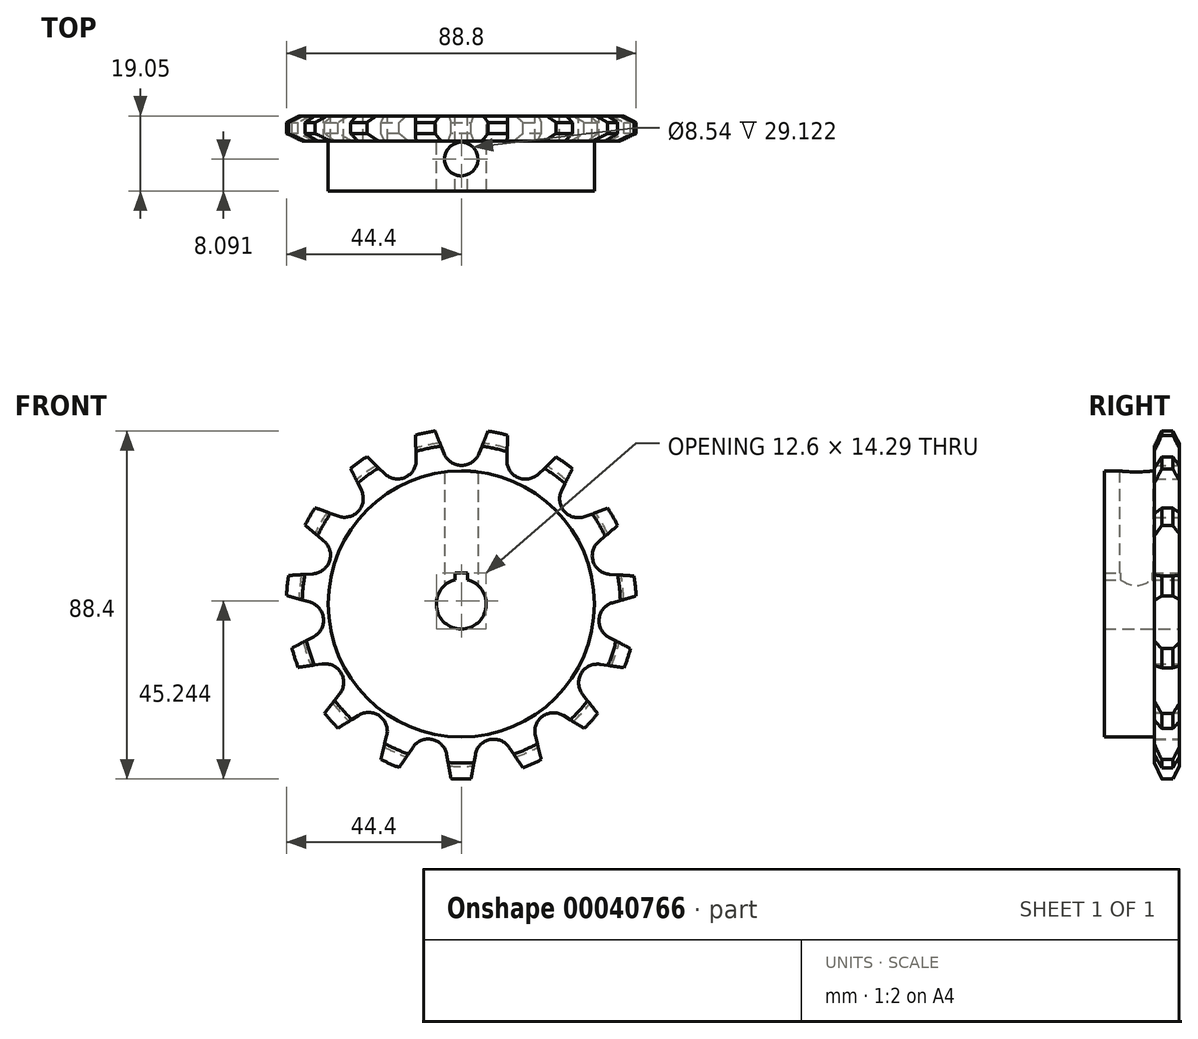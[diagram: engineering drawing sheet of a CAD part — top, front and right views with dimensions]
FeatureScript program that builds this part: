
annotation { "Feature Type Name" : "Feature", "Feature Type Description" : "" }
export const myFeature = defineFeature(function(context is Context, id is Id, definition is map)
    precondition{}
    {
        {
            var Q0;
            Q0=qCreatedBy(makeId("Front.planeOp"),FACE);
            var sketch = newSketch(context, id + "F0", { "sketchPlane" : qUnion([Q0])});
            skArc(sketch, "E0", {"start": v(-6.66, 43.95) * mm, "mid": v(-9.18, 43.5) * mm, "end": v(-11.66, 42.9) * mm});
            skArc(sketch, "E1", {"start": v(-4.34, 38.18) * mm, "mid": v(0.07, 35.2) * mm, "end": v(4.48, 38.18) * mm});
            skLineSegment(sketch, "E2", {"start": v(4.48, 38.18) * mm, "end": v(6.79, 43.93) * mm});
            skLineSegment(sketch, "E3", {"start": v(-4.34, 38.18) * mm, "end": v(-6.66, 43.95) * mm});
            skLineSegment(sketch, "E4.1.0", {"start": v(-19.5, 33.12) * mm, "end": v(-23.96, 37.44) * mm});
            skArc(sketch, "E4.1.1", {"start": v(-19.5, 33.12) * mm, "mid": v(-14.26, 32.19) * mm, "end": v(-11.44, 36.7) * mm});
            skLineSegment(sketch, "E4.1.2", {"start": v(-11.44, 36.7) * mm, "end": v(-11.66, 42.9) * mm});
            skLineSegment(sketch, "E4.2.0", {"start": v(-31.28, 22.32) * mm, "end": v(-37.12, 24.45) * mm});
            skArc(sketch, "E4.2.1", {"start": v(-31.28, 22.32) * mm, "mid": v(-26.12, 23.6) * mm, "end": v(-25.38, 28.88) * mm});
            skLineSegment(sketch, "E4.2.2", {"start": v(-25.38, 28.88) * mm, "end": v(-28.1, 34.44) * mm});
            skLineSegment(sketch, "E4.3.0", {"start": v(-37.66, 7.67) * mm, "end": v(-43.86, 7.24) * mm});
            skArc(sketch, "E4.3.1", {"start": v(-37.66, 7.67) * mm, "mid": v(-33.46, 10.94) * mm, "end": v(-34.93, 16.06) * mm});
            skLineSegment(sketch, "E4.3.2", {"start": v(-34.93, 16.06) * mm, "end": v(-39.68, 20.03) * mm});
            skLineSegment(sketch, "E4.4.0", {"start": v(-37.52, -8.31) * mm, "end": v(-43.01, -11.22) * mm});
            skArc(sketch, "E4.4.1", {"start": v(-37.52, -8.31) * mm, "mid": v(-35.02, -3.61) * mm, "end": v(-38.44, 0.46) * mm});
            skLineSegment(sketch, "E4.4.2", {"start": v(-38.44, 0.46) * mm, "end": v(-44.4, 2.16) * mm});
            skLineSegment(sketch, "E4.5.0", {"start": v(-30.9, -22.85) * mm, "end": v(-34.73, -27.75) * mm});
            skArc(sketch, "E4.5.1", {"start": v(-30.9, -22.85) * mm, "mid": v(-30.52, -17.55) * mm, "end": v(-35.3, -15.22) * mm});
            skLineSegment(sketch, "E4.5.2", {"start": v(-35.3, -15.22) * mm, "end": v(-41.44, -16.08) * mm});
            skLineSegment(sketch, "E4.6.0", {"start": v(-18.93, -33.44) * mm, "end": v(-20.44, -39.47) * mm});
            skArc(sketch, "E4.6.1", {"start": v(-18.93, -33.44) * mm, "mid": v(-20.75, -28.44) * mm, "end": v(-26.06, -28.26) * mm});
            skLineSegment(sketch, "E4.6.2", {"start": v(-26.06, -28.26) * mm, "end": v(-31.31, -31.55) * mm});
            skLineSegment(sketch, "E4.7.0", {"start": v(-3.7, -38.25) * mm, "end": v(-2.62, -44.37) * mm});
            skArc(sketch, "E4.7.1", {"start": v(-3.7, -38.25) * mm, "mid": v(-7.38, -34.42) * mm, "end": v(-12.32, -36.42) * mm});
            skLineSegment(sketch, "E4.7.2", {"start": v(-12.32, -36.42) * mm, "end": v(-15.77, -41.56) * mm});
            skLineSegment(sketch, "E4.8.0", {"start": v(12.19, -36.45) * mm, "end": v(15.66, -41.6) * mm});
            skArc(sketch, "E4.8.1", {"start": v(12.19, -36.45) * mm, "mid": v(7.25, -34.45) * mm, "end": v(3.56, -38.28) * mm});
            skLineSegment(sketch, "E4.8.2", {"start": v(3.56, -38.28) * mm, "end": v(2.5, -44.38) * mm});
            skLineSegment(sketch, "E4.9.0", {"start": v(25.96, -28.34) * mm, "end": v(31.22, -31.64) * mm});
            skArc(sketch, "E4.9.1", {"start": v(25.96, -28.34) * mm, "mid": v(20.64, -28.52) * mm, "end": v(18.82, -33.52) * mm});
            skLineSegment(sketch, "E4.9.2", {"start": v(18.82, -33.52) * mm, "end": v(20.33, -39.53) * mm});
            skLineSegment(sketch, "E4.10.0", {"start": v(35.24, -15.33) * mm, "end": v(41.4, -16.2) * mm});
            skArc(sketch, "E4.10.1", {"start": v(35.24, -15.33) * mm, "mid": v(30.46, -17.66) * mm, "end": v(30.83, -22.97) * mm});
            skLineSegment(sketch, "E4.10.2", {"start": v(30.83, -22.97) * mm, "end": v(34.65, -27.84) * mm});
            skLineSegment(sketch, "E4.11.0", {"start": v(38.43, 0.33) * mm, "end": v(44.4, 2.03) * mm});
            skArc(sketch, "E4.11.1", {"start": v(38.43, 0.33) * mm, "mid": v(35, -3.75) * mm, "end": v(37.5, -8.44) * mm});
            skLineSegment(sketch, "E4.11.2", {"start": v(37.5, -8.44) * mm, "end": v(42.98, -11.34) * mm});
            skLineSegment(sketch, "E4.12.0", {"start": v(34.97, 15.93) * mm, "end": v(39.74, 19.92) * mm});
            skArc(sketch, "E4.12.1", {"start": v(34.97, 15.93) * mm, "mid": v(33.5, 10.82) * mm, "end": v(37.7, 7.54) * mm});
            skLineSegment(sketch, "E4.12.2", {"start": v(37.7, 7.54) * mm, "end": v(43.88, 7.12) * mm});
            skLineSegment(sketch, "E4.13.0", {"start": v(25.47, 28.78) * mm, "end": v(28.2, 34.36) * mm});
            skArc(sketch, "E4.13.1", {"start": v(25.47, 28.78) * mm, "mid": v(26.2, 23.5) * mm, "end": v(31.37, 22.22) * mm});
            skLineSegment(sketch, "E4.13.2", {"start": v(31.37, 22.22) * mm, "end": v(37.19, 24.35) * mm});
            skLineSegment(sketch, "E4.14.0", {"start": v(11.56, 36.65) * mm, "end": v(11.79, 42.86) * mm});
            skArc(sketch, "E4.14.1", {"start": v(11.56, 36.65) * mm, "mid": v(14.38, 32.13) * mm, "end": v(19.62, 33.06) * mm});
            skLineSegment(sketch, "E4.14.2", {"start": v(19.62, 33.06) * mm, "end": v(24.07, 37.37) * mm});
            skArc(sketch, "E5.trimOffspring", {"start": v(-23.96, 37.44) * mm, "mid": v(-26.08, 36) * mm, "end": v(-28.1, 34.44) * mm});
            skArc(sketch, "E6.trimOffspring", {"start": v(-37.12, 24.45) * mm, "mid": v(-38.46, 22.28) * mm, "end": v(-39.68, 20.03) * mm});
            skArc(sketch, "E7.trimOffspring", {"start": v(11.79, 42.86) * mm, "mid": v(9.3, 43.47) * mm, "end": v(6.79, 43.93) * mm});
            skArc(sketch, "E8.trimOffspring", {"start": v(28.2, 34.36) * mm, "mid": v(26.18, 35.92) * mm, "end": v(24.07, 37.37) * mm});
            skArc(sketch, "E9.trimOffspring", {"start": v(39.74, 19.92) * mm, "mid": v(38.53, 22.17) * mm, "end": v(37.19, 24.35) * mm});
            skArc(sketch, "E10.trimOffspring", {"start": v(44.4, 2.03) * mm, "mid": v(44.21, 4.58) * mm, "end": v(43.88, 7.12) * mm});
            skArc(sketch, "E11.trimOffspring", {"start": v(41.4, -16.2) * mm, "mid": v(42.25, -13.8) * mm, "end": v(42.98, -11.34) * mm});
            skArc(sketch, "E12.trimOffspring", {"start": v(31.22, -31.64) * mm, "mid": v(33, -29.79) * mm, "end": v(34.65, -27.84) * mm});
            skArc(sketch, "E13.trimOffspring", {"start": v(15.66, -41.6) * mm, "mid": v(18.02, -40.63) * mm, "end": v(20.33, -39.53) * mm});
            skArc(sketch, "E14.trimOffspring", {"start": v(-2.62, -44.37) * mm, "mid": v(-0.06, -44.45) * mm, "end": v(2.5, -44.38) * mm});
            skArc(sketch, "E15.trimOffspring", {"start": v(-20.44, -39.47) * mm, "mid": v(-18.14, -40.58) * mm, "end": v(-15.77, -41.56) * mm});
            skArc(sketch, "E16.trimOffspring", {"start": v(-34.73, -27.75) * mm, "mid": v(-33.07, -29.7) * mm, "end": v(-31.31, -31.55) * mm});
            skArc(sketch, "E17.trimOffspring", {"start": v(-43.01, -11.22) * mm, "mid": v(-42.3, -13.68) * mm, "end": v(-41.44, -16.08) * mm});
            skArc(sketch, "E18.trimOffspring", {"start": v(-43.86, 7.24) * mm, "mid": v(-44.2, 4.7) * mm, "end": v(-44.4, 2.16) * mm});
            skSolve(sketch);
        }
        {
            var Q0;
            Q0 = qSketchRegion(id + "F0", true);
            extrude(context, id + "F1", {"entities" : qUnion([Q0]), "depth" : 6.35 * mm});
        }
        {
            var Q0;
            Q0=qCreatedBy(makeId("Right.planeOp"),FACE);
            var sketch = newSketch(context, id + "F2", { "sketchPlane" : qUnion([Q0])});
            skLineSegment(sketch, "E19", {"start": v(-4.11, 45.22) * mm, "end": v(-2.04, 45.22) * mm});
            skLineSegment(sketch, "E20", {"start": v(-2.04, 45.22) * mm, "end": v(0.8, 39.7) * mm});
            skLineSegment(sketch, "E21", {"start": v(-4.11, 45.22) * mm, "end": v(-7.04, 38.94) * mm});
            skLineSegment(sketch, "E22", {"start": v(-7.04, 38.94) * mm, "end": v(-6.55, 46.64) * mm});
            skLineSegment(sketch, "E23", {"start": v(-6.55, 46.64) * mm, "end": v(0.85, 46.64) * mm});
            skLineSegment(sketch, "E24", {"start": v(0.85, 46.64) * mm, "end": v(0.8, 39.7) * mm});
            skLineSegment(sketch, "E25", {"start": v(0, 0) * mm, "end": v(46.05, 0) * mm});
            skSolve(sketch);
        }
        {
            var Q0;
            Q0 = qSketchRegion(id + "F2", true);
            var Q1;
            Q1=sQuery(id+"F2.wireOp",EDGE,"E25");
            revolve(context, id + "F3", {"operationType" : NewBodyOperationType.REMOVE, "entities" : qUnion([Q0]), "axis" : qUnion([Q1]), "revolveType" : RevolveType.FULL, "oppositeDirection" : true});
        }
        {
            var Q0;
            Q0=qCreatedBy(makeId("Front.planeOp"),FACE);
            var sketch = newSketch(context, id + "F4", { "sketchPlane" : qUnion([Q0])});
            skCircle(sketch, "E26", {"center": v(0, 0) * mm, "radius": 6.35 * mm});
            skLineSegment(sketch, "E27.rect.top", {"start": v(1.59, 7.94) * mm, "end": v(-1.59, 7.94) * mm});
            skLineSegment(sketch, "E27.rect.left", {"start": v(1.59, 6.15) * mm, "end": v(1.59, 7.94) * mm});
            skLineSegment(sketch, "E27.rect.right", {"start": v(-1.59, 6.15) * mm, "end": v(-1.59, 7.94) * mm});
            skPoint(sketch, "E27.rect.middle", {"position": v(0, 6.35) * mm});
            skPoint(sketch, "E28.orphan", {"position": v(-1.59, 4.76) * mm});
            skPoint(sketch, "E29.orphan", {"position": v(1.59, 4.76) * mm});
            skSolve(sketch);
        }
        {
            var Q0;
            Q0 = qSketchRegion(id + "F4", true);
            extrude(context, id + "F5", {"entities" : qUnion([Q0]), "operationType" : NewBodyOperationType.REMOVE, "depth" : 43.24 * mm});
        }
        {
            var Q0;
            Q0=makeQuery(id+"F1.opExtrude","CAP_FACE",FACE,{"disambiguationData":[OSD([sQuery(id+"F0.wireOp",EDGE,"E0"),sQuery(id+"F0.wireOp",EDGE,"E1"),sQuery(id+"F0.wireOp",EDGE,"E2"),sQuery(id+"F0.wireOp",EDGE,"E3"),sQuery(id+"F0.wireOp",EDGE,"E4.1.0"),sQuery(id+"F0.wireOp",EDGE,"E4.1.1"),sQuery(id+"F0.wireOp",EDGE,"E4.1.2"),sQuery(id+"F0.wireOp",EDGE,"E4.2.0"),sQuery(id+"F0.wireOp",EDGE,"E4.2.1"),sQuery(id+"F0.wireOp",EDGE,"E4.2.2"),sQuery(id+"F0.wireOp",EDGE,"E4.3.0"),sQuery(id+"F0.wireOp",EDGE,"E4.3.1"),sQuery(id+"F0.wireOp",EDGE,"E4.3.2"),sQuery(id+"F0.wireOp",EDGE,"E4.4.0"),sQuery(id+"F0.wireOp",EDGE,"E4.4.1"),sQuery(id+"F0.wireOp",EDGE,"E4.4.2"),sQuery(id+"F0.wireOp",EDGE,"E4.5.0"),sQuery(id+"F0.wireOp",EDGE,"E4.5.1"),sQuery(id+"F0.wireOp",EDGE,"E4.5.2"),sQuery(id+"F0.wireOp",EDGE,"E4.6.0"),sQuery(id+"F0.wireOp",EDGE,"E4.6.1"),sQuery(id+"F0.wireOp",EDGE,"E4.6.2"),sQuery(id+"F0.wireOp",EDGE,"E4.7.0"),sQuery(id+"F0.wireOp",EDGE,"E4.7.1"),sQuery(id+"F0.wireOp",EDGE,"E4.7.2"),sQuery(id+"F0.wireOp",EDGE,"E4.8.0"),sQuery(id+"F0.wireOp",EDGE,"E4.8.1"),sQuery(id+"F0.wireOp",EDGE,"E4.8.2"),sQuery(id+"F0.wireOp",EDGE,"E4.9.0"),sQuery(id+"F0.wireOp",EDGE,"E4.9.1"),sQuery(id+"F0.wireOp",EDGE,"E4.9.2"),sQuery(id+"F0.wireOp",EDGE,"E4.10.0"),sQuery(id+"F0.wireOp",EDGE,"E4.10.1"),sQuery(id+"F0.wireOp",EDGE,"E4.10.2"),sQuery(id+"F0.wireOp",EDGE,"E4.11.0"),sQuery(id+"F0.wireOp",EDGE,"E4.11.1"),sQuery(id+"F0.wireOp",EDGE,"E4.11.2"),sQuery(id+"F0.wireOp",EDGE,"E4.12.0"),sQuery(id+"F0.wireOp",EDGE,"E4.12.1"),sQuery(id+"F0.wireOp",EDGE,"E4.12.2"),sQuery(id+"F0.wireOp",EDGE,"E4.13.0"),sQuery(id+"F0.wireOp",EDGE,"E4.13.1"),sQuery(id+"F0.wireOp",EDGE,"E4.13.2"),sQuery(id+"F0.wireOp",EDGE,"E4.14.0"),sQuery(id+"F0.wireOp",EDGE,"E4.14.1"),sQuery(id+"F0.wireOp",EDGE,"E4.14.2"),sQuery(id+"F0.wireOp",EDGE,"E5.trimOffspring"),sQuery(id+"F0.wireOp",EDGE,"E6.trimOffspring"),sQuery(id+"F0.wireOp",EDGE,"E7.trimOffspring"),sQuery(id+"F0.wireOp",EDGE,"E8.trimOffspring"),sQuery(id+"F0.wireOp",EDGE,"E9.trimOffspring"),sQuery(id+"F0.wireOp",EDGE,"E10.trimOffspring"),sQuery(id+"F0.wireOp",EDGE,"E11.trimOffspring"),sQuery(id+"F0.wireOp",EDGE,"E12.trimOffspring"),sQuery(id+"F0.wireOp",EDGE,"E13.trimOffspring"),sQuery(id+"F0.wireOp",EDGE,"E14.trimOffspring"),sQuery(id+"F0.wireOp",EDGE,"E15.trimOffspring"),sQuery(id+"F0.wireOp",EDGE,"E16.trimOffspring"),sQuery(id+"F0.wireOp",EDGE,"E17.trimOffspring"),sQuery(id+"F0.wireOp",EDGE,"E18.trimOffspring")])],"isStart":false});
            var sketch = newSketch(context, id + "F6", { "sketchPlane" : qUnion([Q0])});
            skCircle(sketch, "E30", {"center": v(0, 0) * mm, "radius": 33.82 * mm});
            skSolve(sketch);
        }
        {
            var Q0;
            Q0=makeQuery(id+"F6.imprint","IMPRINT",FACE,{"disambiguationData":[TD([[makeQuery(id+"F6.imprint","IMPRINT",EDGE,{"derivedFrom":sQuery(id+"F6.wireOp",EDGE,"E30")}),1.0]])]});
            extrude(context, id + "F7", {"entities" : qUnion([Q0]), "operationType" : NewBodyOperationType.ADD, "depth" : 12.7 * mm});
        }
        {
            var Q0;
            Q0=qCreatedBy(makeId("Top.planeOp"),FACE);
            var sketch = newSketch(context, id + "F8", { "sketchPlane" : qUnion([Q0])});
            skLineSegment(sketch, "E31", {"start": v(0, -17.15) * mm, "end": v(0, -4.76) * mm});
            skCircle(sketch, "E32", {"center": v(0, -10.96) * mm, "radius": 4.27 * mm});
            skSolve(sketch);
        }
        {
            var Q0;
            Q0 = qSketchRegion(id + "F8", true);
            extrude(context, id + "F9", {"entities" : qUnion([Q0]), "operationType" : NewBodyOperationType.REMOVE, "depth" : 59.6 * mm});
        }
    });
